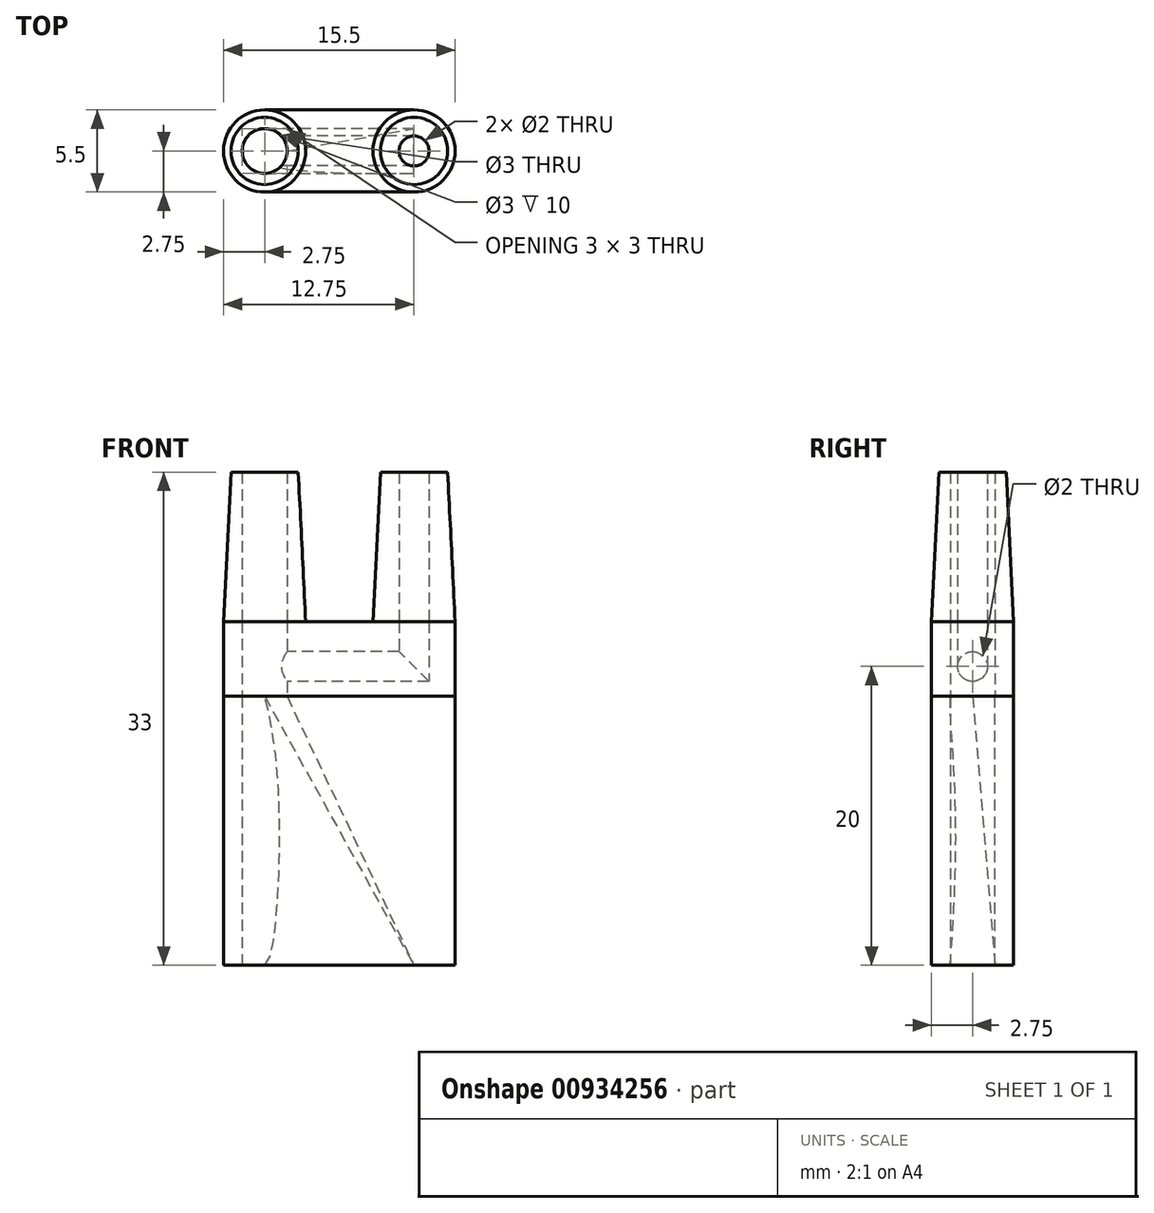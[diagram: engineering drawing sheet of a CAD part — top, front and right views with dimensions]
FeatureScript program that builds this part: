
annotation { "Feature Type Name" : "Feature", "Feature Type Description" : "" }
export const myFeature = defineFeature(function(context is Context, id is Id, definition is map)
    precondition{}
    {
        {
            var Q0;
            Q0=qCreatedBy(makeId("Front.planeOp"),FACE);
            var sketch = newSketch(context, id + "F0", { "sketchPlane" : qUnion([Q0])});
            skLineSegment(sketch, "E0", {"start": v(0, 0) * mm, "end": v(2.75, 0) * mm});
            skLineSegment(sketch, "E1", {"start": v(2.75, 0) * mm, "end": v(2.25, 10) * mm});
            skLineSegment(sketch, "E2", {"start": v(2.25, 10) * mm, "end": v(0, 10) * mm});
            skLineSegment(sketch, "E3", {"start": v(0, 10) * mm, "end": v(0, 0) * mm});
            skSolve(sketch);
        }
        {
            var Q0;
            Q0=makeQuery(id+"F0.imprint","IMPRINT",FACE,{"disambiguationData":[TD([[makeQuery(id+"F0.imprint","IMPRINT",EDGE,{"derivedFrom":sQuery(id+"F0.wireOp",EDGE,"E0")}),1.0]])]});
            var Q1;
            Q1=sQuery(id+"F0.wireOp",EDGE,"E3");
            revolve(context, id + "F1", {"surfaceOperationType" : NewSurfaceOperationType.NEW, "entities" : qUnion([Q0]), "axis" : qUnion([Q1]), "revolveType" : RevolveType.FULL});
        }
        {
            var Q0;
            Q0=qCreatedBy(makeId("Front.planeOp"),FACE);
            var sketch = newSketch(context, id + "F2", { "sketchPlane" : qUnion([Q0])});
            skLineSegment(sketch, "E4", {"start": v(0, 0) * mm, "end": v(0, 10) * mm});
            skLineSegment(sketch, "E5", {"start": v(0, 0) * mm, "end": v(0, -23) * mm});
            skLineSegment(sketch, "E6", {"start": v(0, -3) * mm, "end": v(10, -3) * mm});
            skLineSegment(sketch, "E7", {"start": v(10, 10) * mm, "end": v(10, -3) * mm});
            skLineSegment(sketch, "E8", {"start": v(10, -3) * mm, "end": v(10, 0) * mm});
            skSolve(sketch);
        }
        {
            var Q0;
            Q0=makeQuery(id+"F1.opRevolve","SWEPT_BODY",BODY,{"disambiguationData":[OSD([sQuery(id+"F0.wireOp",EDGE,"E0"),sQuery(id+"F0.wireOp",EDGE,"E1"),sQuery(id+"F0.wireOp",EDGE,"E2"),sQuery(id+"F0.wireOp",EDGE,"E3")])]});
            var Q1;
            Q1=sQuery(id+"F2.wireOp",VERTEX,"E4.start");
            var Q2;
            Q2=sQuery(id+"F2.wireOp",VERTEX,"E8.end");
            transform(context, id + "F3", {"entities" : qUnion([Q0]), "transformType" : TransformType.TRANSLATION_ENTITY, "oppositeDirectionEntity" : false, "transformLine" : qUnion([Q1, Q2]), "makeCopy" : true});
        }
        {
            var Q0;
            Q0=makeQuery(id+"F1.opRevolve","SWEPT_FACE",FACE,{"disambiguationData":[OSD([sQuery(id+"F0.wireOp",EDGE,"E2")])]});
            var sketch = newSketch(context, id + "F4", { "sketchPlane" : qUnion([Q0])});
            skCircle(sketch, "E9", {"center": v(0, 0) * mm, "radius": 1.5 * mm});
            skSolve(sketch);
        }
        {
            var Q0;
            Q0=makeQuery(id+"F3.opPattern","COPY",FACE,{"derivedFrom":makeQuery(id+"F1.opRevolve","SWEPT_FACE",FACE,{"disambiguationData":[OSD([sQuery(id+"F0.wireOp",EDGE,"E2")])]}),"instanceName":"1"});
            var sketch = newSketch(context, id + "F5", { "sketchPlane" : qUnion([Q0])});
            skCircle(sketch, "E10", {"center": v(10, 0) * mm, "radius": 1 * mm});
            skSolve(sketch);
        }
        {
            var Q0;
            Q0=qCreatedBy(makeId("Top.planeOp"),FACE);
            var sketch = newSketch(context, id + "F6", { "sketchPlane" : qUnion([Q0])});
            skArc(sketch, "E11", {"start": v(0, 2.75) * mm, "mid": v(-2.75, 0) * mm, "end": v(0, -2.75) * mm});
            skArc(sketch, "E12", {"start": v(10, -2.75) * mm, "mid": v(12.75, 0) * mm, "end": v(10, 2.75) * mm});
            skLineSegment(sketch, "E13", {"start": v(0, 2.75) * mm, "end": v(10, 2.75) * mm});
            skLineSegment(sketch, "E14", {"start": v(10, -2.75) * mm, "end": v(0, -2.75) * mm});
            skSolve(sketch);
        }
        {
            var Q0;
            Q0=makeQuery(id+"F6.imprint","IMPRINT",FACE,{"disambiguationData":[TD([[makeQuery(id+"F6.imprint","IMPRINT",EDGE,{"derivedFrom":sQuery(id+"F6.wireOp",EDGE,"E11")}),1.0]])]});
            extrude(context, id + "F7", {"entities" : qUnion([Q0]), "oppositeDirection" : true, "depth" : 5 * mm, "offsetDistance" : 25 * mm});
        }
        {
            var Q0;
            Q0=makeQuery(id+"F7.opExtrude","CAP_FACE",FACE,{"disambiguationData":[OSD([sQuery(id+"F6.wireOp",EDGE,"E11"),sQuery(id+"F6.wireOp",EDGE,"E12"),sQuery(id+"F6.wireOp",EDGE,"E13"),sQuery(id+"F6.wireOp",EDGE,"E14")])],"isStart":false});
            var Q1;
            Q1 = qSketchRegion(id + "F4", true);
            extrude(context, id + "F8", {"entities" : qUnion([Q0, Q1]), "depth" : 18 * mm, "offsetDistance" : 25 * mm});
        }
        {
            var Q0;
            Q0=makeQuery(id+"F5.imprint","IMPRINT",FACE,{"disambiguationData":[TD([[makeQuery(id+"F5.imprint","IMPRINT",EDGE,{"derivedFrom":sQuery(id+"F5.wireOp",EDGE,"E10")}),1.0]])]});
            var Q1;
            Q1=sQuery(id+"F2.wireOp",EDGE,"E7");
            var Q2;
            Q2=sQuery(id+"F2.wireOp",EDGE,"E6");
            sweep(context, id + "F9", {"operationType" : NewBodyOperationType.REMOVE, "profiles" : qUnion([Q0]), "path" : qUnion([Q1, Q2])});
        }
        {
            var Q0;
            Q0=makeQuery(id+"F4.imprint","IMPRINT",FACE,{"disambiguationData":[TD([[makeQuery(id+"F4.imprint","IMPRINT",EDGE,{"derivedFrom":sQuery(id+"F4.wireOp",EDGE,"E9")}),1.0]])]});
            var Q1;
            Q1=sQuery(id+"F2.wireOp",EDGE,"E4");
            var Q2;
            Q2=sQuery(id+"F2.wireOp",EDGE,"E5");
            sweep(context, id + "F10", {"operationType" : NewBodyOperationType.REMOVE, "profiles" : qUnion([Q0]), "path" : qUnion([Q1, Q2])});
        }
        {
            var Q0;
            Q0=makeQuery(id+"F7.opExtrude","CAP_FACE",FACE,{"disambiguationData":[OSD([sQuery(id+"F6.wireOp",EDGE,"E11"),sQuery(id+"F6.wireOp",EDGE,"E12"),sQuery(id+"F6.wireOp",EDGE,"E13"),sQuery(id+"F6.wireOp",EDGE,"E14")])],"isStart":false});
            var sketch = newSketch(context, id + "F11", { "sketchPlane" : qUnion([Q0])});
            skCircle(sketch, "E15", {"center": v(0, 0) * mm, "radius": 1.5 * mm});
            skSolve(sketch);
        }
        {
            var Q0;
            Q0=makeQuery(id+"F8.opExtrude","CAP_FACE",FACE,{"disambiguationData":[OSD([sQuery(id+"F6.wireOp",EDGE,"E11"),sQuery(id+"F6.wireOp",EDGE,"E12"),sQuery(id+"F6.wireOp",EDGE,"E13"),sQuery(id+"F6.wireOp",EDGE,"E14")])],"isStart":false});
            var sketch = newSketch(context, id + "F12", { "sketchPlane" : qUnion([Q0])});
            skLineSegment(sketch, "E16", {"start": v(0, -1.5) * mm, "end": v(0, 1.5) * mm});
            skLineSegment(sketch, "E17", {"start": v(0, 1.5) * mm, "end": v(10, 1.5) * mm});
            skLineSegment(sketch, "E18", {"start": v(10, 1.5) * mm, "end": v(10, -1.5) * mm});
            skLineSegment(sketch, "E19", {"start": v(10, -1.5) * mm, "end": v(0, -1.5) * mm});
            skSolve(sketch);
        }
        {
            var Q0;
            Q0 = qSketchRegion(id + "F11", true);
            var Q1;
            Q1 = qSketchRegion(id + "F12", true);
            loft(context, id + "F13", {"operationType" : NewBodyOperationType.REMOVE, "sheetProfilesArray" : [{ "sheetProfileEntities" : qUnion([Q0]) }, { "sheetProfileEntities" : qUnion([Q1]) }]});
        }
    });
